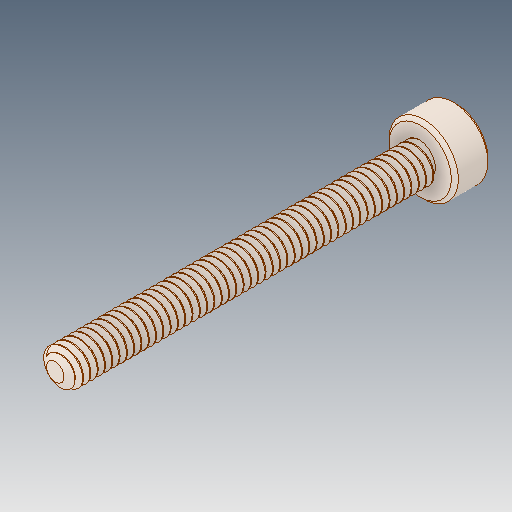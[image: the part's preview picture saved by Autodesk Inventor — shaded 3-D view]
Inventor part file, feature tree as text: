
AUTODESK INVENTOR PART (.ipt)
format: ipt  version: 2019 (Build 230136000, 136)  size: 1,315,840 bytes
history: native  units: mm
features: chamfer x1
ambient origin geometry x8: Origin, YZ Plane, XZ Plane, XY Plane, X Axis, Y Axis, Z Axis, Center Point
bodies: Solid1 (feature_tree)
feature tree (1):
  chamfer  "Chamfer1"  [1 undecoded]
note: 1 required parameter value undecoded (feature->parameter linkage not recoverable at this tier; creation-order binding heuristic only, values carry confidence <= 0.55)
